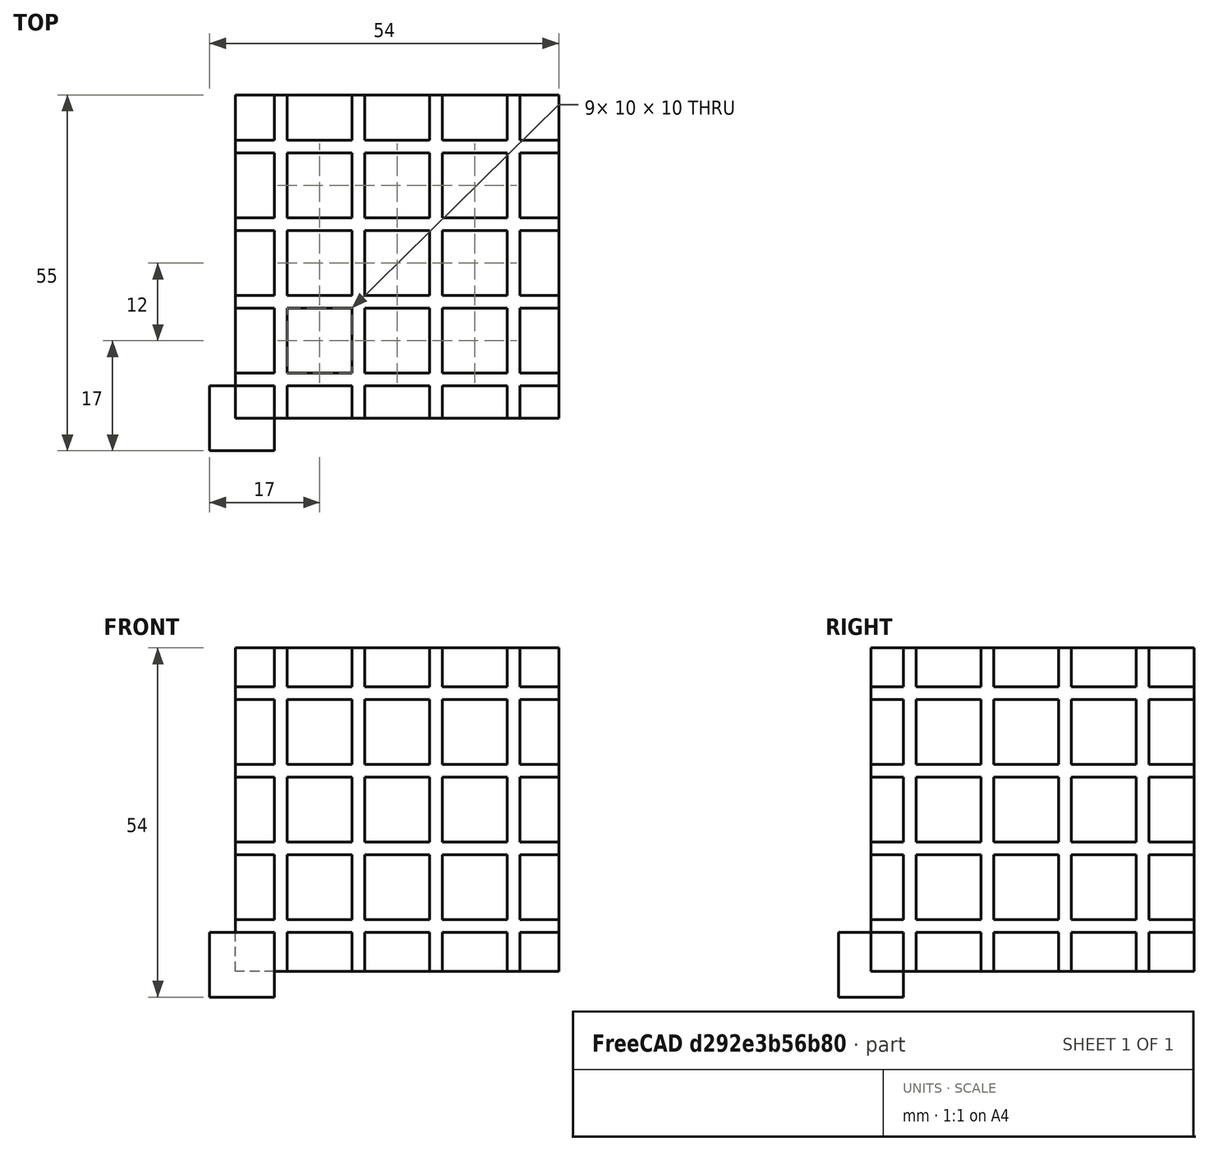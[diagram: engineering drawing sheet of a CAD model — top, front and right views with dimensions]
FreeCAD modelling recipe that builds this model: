
FCSTD DOCUMENT  (FreeCAD 0.21R33694 (Git))
Label: OJT1_T10P01.peka
License: All rights reserved
LicenseURL: http://en.wikipedia.org/wiki/All_rights_reserved
objects: Part::Box×2, Part::FeaturePython×1, Part::Cut×1
note: 3 computed .brp shape members not serialized (recipe doc carries the construction recipe); baked Part::Feature solids carry a one-line shape summary decoded from their .brp

FEATURE [Part::Box] Box  label="Cub"
  AttacherType = Attacher::AttachEngine3D
  Height = 10
  Length = 10
  Width = 10
FEATURE [Part::FeaturePython] Array  # Draft array (typed FeaturePython)
  AlwaysSyncPlacement = false
  Angle = 360
  ArrayType = 0
  Axis = (0,0,1)
  Base = -> Box
  Center = (0,0,0)
  Count = 125
  ExpandArray = false
  Fuse = false
  IntervalAxis = (0,0,0)
  IntervalX = (12,0,0)
  IntervalY = (0,12,0)
  IntervalZ = (0,0,12)
  NumberCircles = 3
  NumberPolar = 5
  NumberX = 5
  NumberY = 5
  NumberZ = 5
  PlacementList = 125 placements: [(0,0,0),(0,0,12),(0,0,24),(0,0,36),(0,0,48),(0,12,0),(0,12,12),(0,12,24),(0,12,36),(0,12,48),(0,24,0),(0,24,12),(0,24,24),(0,24,36),(0,24,48),(0,36,0),(0,36,12),(0,36,24),(0,36,36),(0,36,48),(0,48,0),(0,48,12),(0,48,24),(0,48,36),(0,48,48),(12,0,0),(12,0,12),(12,0,24),(12,0,36),(12,0,48),(12,12,0),(12,12,12),(12,12,24),(12,12,36),(12,12,48),(12,24,0),(12,24,12),(12,24,24),(12,24,36),(12,24,48),+85 more]
  RadialDistance = 50
  ScaleList = (125) [(1,1,1),(1,1,1),(1,1,1),(1,1,1),(1,1,1),(1,1,1),(1,1,1),(1,1,1),(1,1,1),(1,1,1),(1,1,1),(1,1,1),(1,1,1),(1,1,1),(1,1,1),(1,1,1),(1,1,1),(1,1,1),+107 more]
  Symmetry = 1
  TangentialDistance = 25
FEATURE [Part::Box] Box001  label="Cub001"
  AttacherType = Attacher::AttachEngine3D
  Height = 50
  Length = 50
  Placement = pos=(4,5,4) rot=(0,0,1;0rad)
  Width = 50
FEATURE [Part::Cut] Cut
  Base = -> Box001
  Refine = true
  Tool = -> Array
